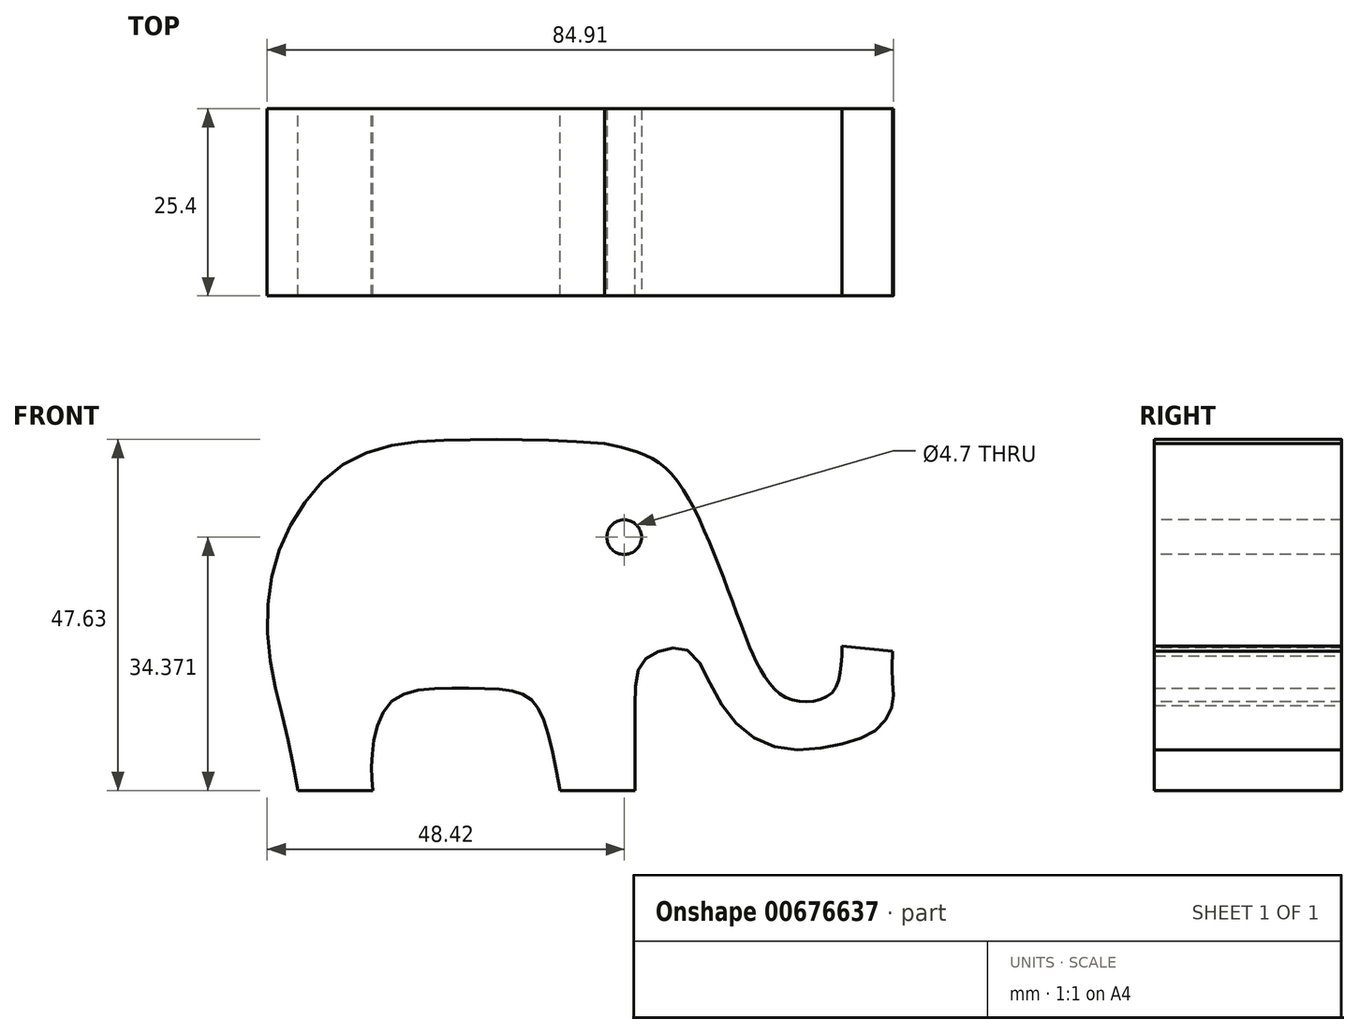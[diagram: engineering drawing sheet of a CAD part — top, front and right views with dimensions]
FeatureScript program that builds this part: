
annotation { "Feature Type Name" : "Feature", "Feature Type Description" : "" }
export const myFeature = defineFeature(function(context is Context, id is Id, definition is map)
    precondition{}
    {
        {
            var Q0;
            Q0=qCreatedBy(makeId("Front.planeOp"),FACE);
            var sketch = newSketch(context, id + "F0", { "sketchPlane" : qUnion([Q0])});
            skFitSpline(sketch, "E0", {"points": [v(-35.56, 0) * mm, v(-37.23, 8.44) * mm, v(-39.3, 17.71) * mm, v(-39.3, 28.02) * mm, v(-35.95, 37.03) * mm, v(-29.76, 43.99) * mm, v(-21.52, 47.08) * mm, v(-12.5, 47.6) * mm, v(-3.75, 47.6) * mm, v(6.04, 47.08) * mm], "startDerivative": vector(-12.65, 78.62) * mm, "endDerivative": vector(87.15, -5.72) * mm});
            skFitSpline(sketch, "E1", {"points": [v(10.16, 11.53) * mm, v(10.16, 4.58) * mm, v(10.16, 0) * mm], "startDerivative": vector(0, -13.25) * mm, "endDerivative": vector(0, -9.69) * mm});
            skLineSegment(sketch, "E2", {"start": v(-35.56, 0) * mm, "end": v(-25.4, 0) * mm});
            skLineSegment(sketch, "E3", {"start": v(10.16, 0) * mm, "end": v(0, 0) * mm});
            skFitSpline(sketch, "E4", {"points": [v(-25.4, 0) * mm, v(-25.4, 5.6) * mm, v(-22.55, 12.3) * mm, v(-13.54, 13.85) * mm, v(-5.8, 13.33) * mm, v(-2.72, 10.76) * mm, v(0, 0) * mm], "startDerivative": vector(-2.74, 36.14) * mm, "endDerivative": vector(10.7, -61.43) * mm});
            skFitSpline(sketch, "E5", {"points": [v(6.04, 47.08) * mm, v(11.35, 45.6) * mm, v(15.54, 42.51) * mm, v(20.17, 33.91) * mm, v(24.58, 22.44) * mm], "startDerivative": vector(26.54, -5.76) * mm, "endDerivative": vector(13.7, -37.31) * mm});
            skLineSegment(sketch, "E6", {"start": v(38.25, 18.23) * mm, "end": v(38.25, 19.58) * mm});
            skFitSpline(sketch, "E7", {"points": [v(24.58, 22.44) * mm, v(26.63, 17.47) * mm, v(29.71, 13.2) * mm, v(33.5, 12.03) * mm, v(37.06, 13.45) * mm, v(38.25, 18.23) * mm], "startDerivative": vector(8.64, -23.1) * mm, "endDerivative": vector(2.06, 26.75) * mm});
            skLineSegment(sketch, "E8", {"start": v(45.11, 18.9) * mm, "end": v(38.25, 19.58) * mm});
            skFitSpline(sketch, "E9", {"points": [v(45.11, 18.9) * mm, v(45.11, 14.5) * mm, v(45.11, 11.64) * mm, v(43.33, 8.55) * mm, v(38.47, 6.34) * mm, v(29.21, 5.9) * mm, v(21.93, 11.64) * mm, v(17.52, 18.9) * mm, v(13.55, 18.9) * mm, v(10.9, 16.93) * mm, v(10.16, 11.53) * mm], "startDerivative": vector(-1.24, -51.33) * mm, "endDerivative": vector(-0.72, -61.06) * mm});
            skSolve(sketch);
        }
        {
            var Q0;
            {var subQ1=sQuery(id+"F0.wireOp",EDGE,"E0");Q0=makeQuery(id+"F0.imprint","IMPRINT",FACE,{"disambiguationData":[TD([[makeQuery(id+"F0.imprint","IMPRINT",EDGE,{"derivedFrom":subQ1}),-1.0]])]});}
            extrude(context, id + "F1", {"entities" : qUnion([Q0]), "depth" : 25.4 * mm});
        }
        {
            var Q0;
            Q0=qCreatedBy(makeId("Front.planeOp"),FACE);
            cPlane(context, id + "F2", {"entities" : qUnion([Q0]), "cplaneType" : CPlaneType.OFFSET, "offset" : 25.4 * mm, "width" : 152.4 * mm, "height" : 152.4 * mm});
        }
        {
            var Q0;
            Q0=qCreatedBy(id+"F2.planeOp",FACE);
            var sketch = newSketch(context, id + "F3", { "sketchPlane" : qUnion([Q0])});
            skCircle(sketch, "E10", {"center": v(8.72, 34.37) * mm, "radius": 2.35 * mm});
            skSolve(sketch);
        }
        {
            var Q0;
            Q0=makeQuery(id+"F3.imprint","IMPRINT",FACE,{"disambiguationData":[TD([[makeQuery(id+"F3.imprint","IMPRINT",EDGE,{"derivedFrom":sQuery(id+"F3.wireOp",EDGE,"E10")}),1.0]])]});
            extrude(context, id + "F4", {"entities" : qUnion([Q0]), "operationType" : NewBodyOperationType.REMOVE, "oppositeDirection" : true, "depth" : 50.8 * mm});
        }
    });
